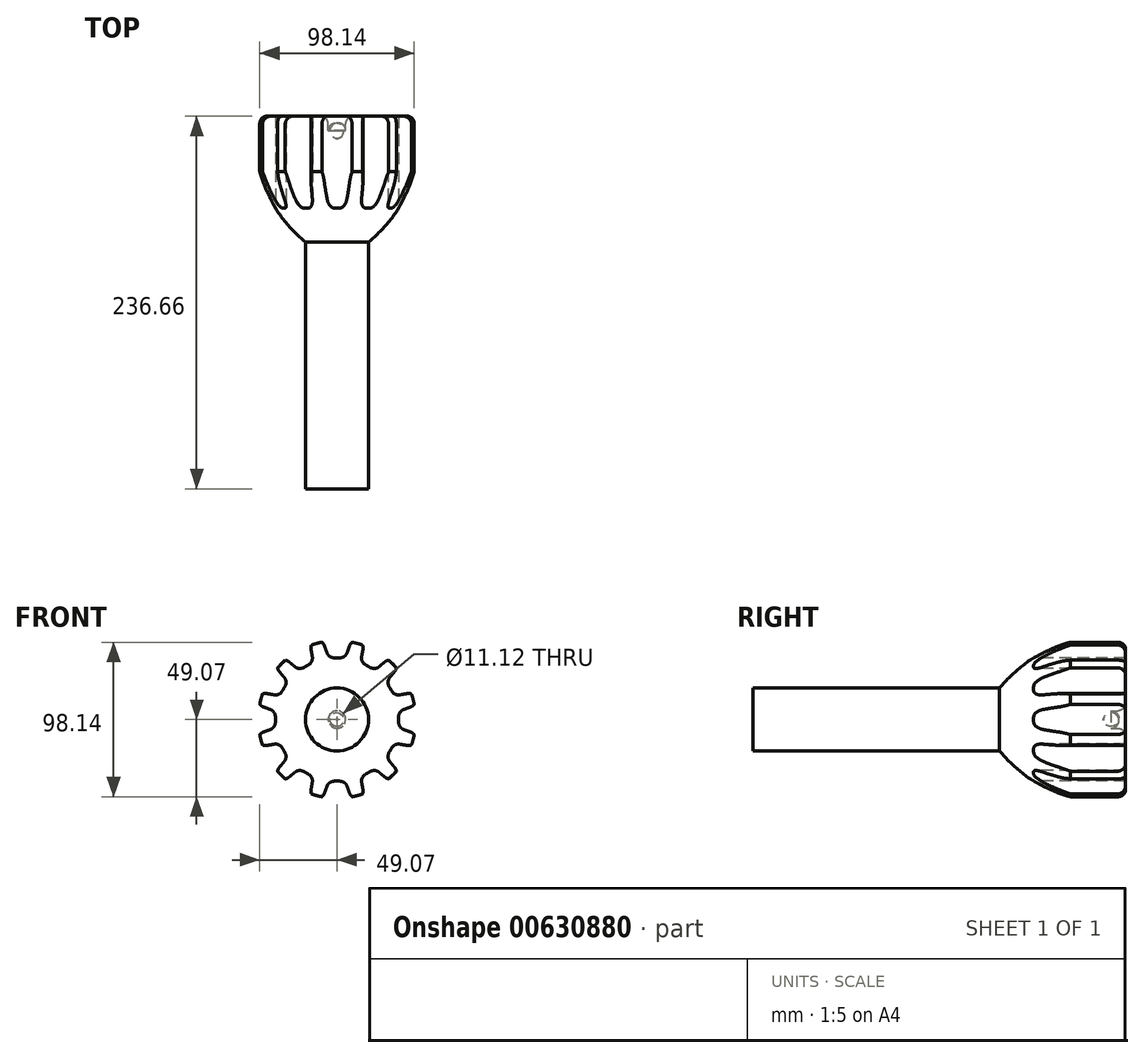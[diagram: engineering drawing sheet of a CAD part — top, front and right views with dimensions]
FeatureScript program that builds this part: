
annotation { "Feature Type Name" : "Feature", "Feature Type Description" : "" }
export const myFeature = defineFeature(function(context is Context, id is Id, definition is map)
    precondition{}
    {
        {
            var Q0;
            Q0=qCreatedBy(makeId("Right.planeOp"),FACE);
            var sketch = newSketch(context, id + "F0", { "sketchPlane" : qUnion([Q0])});
            skLineSegment(sketch, "E0.bottom", {"start": v(78.33, -10) * mm, "end": v(-78.33, -10) * mm});
            skLineSegment(sketch, "E0.top", {"start": v(78.33, 10) * mm, "end": v(-78.33, 10) * mm});
            skLineSegment(sketch, "E0.left", {"start": v(78.33, -10) * mm, "end": v(78.33, 10) * mm});
            skLineSegment(sketch, "E0.right", {"start": v(-78.33, -10) * mm, "end": v(-78.33, 10) * mm});
            skPoint(sketch, "E0.middle", {"position": v(0, 0) * mm});
            skArc(sketch, "E1", {"start": v(123.23, 40) * mm, "mid": v(98.58, 28.3) * mm, "end": v(78.33, 10) * mm});
            skLineSegment(sketch, "E2", {"start": v(123.23, 40) * mm, "end": v(153.33, 40) * mm});
            skLineSegment(sketch, "E3", {"start": v(158.33, 35) * mm, "end": v(158.33, 0.56) * mm});
            skLineSegment(sketch, "E4", {"start": v(153.33, -4.44) * mm, "end": v(149.1, -4.44) * mm});
            skLineSegment(sketch, "E5", {"start": v(144.1, -9.44) * mm, "end": v(144.1, -10) * mm});
            skLineSegment(sketch, "E6", {"start": v(144.1, -10) * mm, "end": v(78.33, -10) * mm});
            skPoint(sketch, "E7.visualSharp", {"position": v(158.33, 40) * mm});
            skArc(sketch, "E7.filletArc", {"start": v(158.33, 35) * mm, "mid": v(156.87, 38.54) * mm, "end": v(153.33, 40) * mm});
            skPoint(sketch, "E8.visualSharp", {"position": v(158.33, -4.44) * mm});
            skArc(sketch, "E8.filletArc", {"start": v(153.33, -4.44) * mm, "mid": v(156.87, -2.98) * mm, "end": v(158.33, 0.56) * mm});
            skPoint(sketch, "E9.visualSharp", {"position": v(144.1, -4.44) * mm});
            skArc(sketch, "E9.filletArc", {"start": v(149.1, -4.44) * mm, "mid": v(145.56, -5.9) * mm, "end": v(144.1, -9.44) * mm});
            skSolve(sketch);
        }
        {
            var Q0;
            Q0 = qSketchRegion(id + "F0", true);
            var Q1;
            Q1=sQuery(id+"F0.wireOp",EDGE,"E0.bottom");
            revolve(context, id + "F1", {"entities" : qUnion([Q0]), "axis" : qUnion([Q1]), "revolveType" : RevolveType.FULL});
        }
        {
            var Q0;
            Q0=qCreatedBy(makeId("Front.planeOp"),FACE);
            var sketch = newSketch(context, id + "F2", { "sketchPlane" : qUnion([Q0])});
            skLineSegment(sketch, "E10", {"start": v(0, 0) * mm, "end": v(0, 14.13) * mm});
            skLineSegment(sketch, "E11", {"start": v(0, 29.15) * mm, "end": v(0, 14.13) * mm});
            skLineSegment(sketch, "E12", {"start": v(0, 29.15) * mm, "end": v(-1.7, 29.15) * mm});
            skLineSegment(sketch, "E13", {"start": v(-6.4, 32.44) * mm, "end": v(-8, 36.84) * mm});
            skLineSegment(sketch, "E14", {"start": v(-17.5, 37.98) * mm, "end": v(0, 51.15) * mm});
            skPoint(sketch, "E15", {"position": v(-17.5, 37.98) * mm});
            skLineSegment(sketch, "E16", {"start": v(-17, 37.7) * mm, "end": v(-17.5, 37.98) * mm});
            skPoint(sketch, "E17.visualSharp", {"position": v(-5.2, 29.15) * mm});
            skArc(sketch, "E17.filletArc", {"start": v(-6.4, 32.44) * mm, "mid": v(-4.57, 30.05) * mm, "end": v(-1.7, 29.15) * mm});
            skPoint(sketch, "E18.visualSharp", {"position": v(-10.37, 43.35) * mm});
            skArc(sketch, "E18.filletArc", {"start": v(-8, 36.84) * mm, "mid": v(-12.23, 40.1) * mm, "end": v(-17, 37.7) * mm});
            skLineSegment(sketch, "E19.MirrorCS", {"start": v(0, 29.15) * mm, "end": v(1.7, 29.15) * mm});
            skArc(sketch, "E20.MirrorCS", {"start": v(6.4, 32.44) * mm, "mid": v(4.57, 30.05) * mm, "end": v(1.7, 29.15) * mm});
            skLineSegment(sketch, "E21.MirrorCS", {"start": v(6.4, 32.44) * mm, "end": v(8, 36.84) * mm});
            skPoint(sketch, "E22.MirrorP", {"position": v(10.37, 43.35) * mm});
            skArc(sketch, "E23.MirrorCS", {"start": v(8, 36.84) * mm, "mid": v(14.64, 39.74) * mm, "end": v(17.2, 32.96) * mm});
            skLineSegment(sketch, "E24.MirrorCS", {"start": v(15.31, 36.72) * mm, "end": v(17.5, 37.98) * mm});
            skLineSegment(sketch, "E25.MirrorCS", {"start": v(17.5, 37.98) * mm, "end": v(0, 51.15) * mm});
            skSolve(sketch);
        }
        {
            var Q0;
            Q0=makeQuery(id+"F2.imprint","IMPRINT",FACE,{"disambiguationData":[TD([[makeQuery(id+"F2.imprint","IMPRINT",EDGE,{"derivedFrom":sQuery(id+"F2.wireOp",EDGE,"E12")}),-1.0]])]});
            extrude(context, id + "F3", {"entities" : qUnion([Q0]), "operationType" : NewBodyOperationType.REMOVE, "oppositeDirection" : true, "depth" : 201.7 * mm, "offsetDistance" : 25 * mm});
        }
        {
            var Q0;
            Q0=makeQuery(id+"F3.boolean.opBoolean","COPY",FACE,{"derivedFrom":makeQuery(id+"F3.opExtrude","SWEPT_FACE",FACE,{"disambiguationData":[OSD([sQuery(id+"F2.wireOp",EDGE,"E18.filletArc")])]})});
            var Q1;
            Q1=makeQuery(id+"F3.boolean.opBoolean","COPY",FACE,{"derivedFrom":makeQuery(id+"F3.opExtrude","SWEPT_FACE",FACE,{"disambiguationData":[OSD([sQuery(id+"F2.wireOp",EDGE,"E13")])]})});
            var Q2;
            Q2=makeQuery(id+"F3.boolean.opBoolean","COPY",FACE,{"derivedFrom":makeQuery(id+"F3.opExtrude","SWEPT_FACE",FACE,{"disambiguationData":[OSD([sQuery(id+"F2.wireOp",EDGE,"E17.filletArc")])]})});
            var Q3;
            Q3=makeQuery(id+"F3.boolean.opBoolean","COPY",FACE,{"derivedFrom":makeQuery(id+"F3.opExtrude","SWEPT_FACE",FACE,{"disambiguationData":[OSD([sQuery(id+"F2.wireOp",EDGE,"E12"),sQuery(id+"F2.wireOp",EDGE,"E19.MirrorCS")])]})});
            var Q4;
            Q4=makeQuery(id+"F3.boolean.opBoolean","COPY",FACE,{"derivedFrom":makeQuery(id+"F3.opExtrude","SWEPT_FACE",FACE,{"disambiguationData":[OSD([sQuery(id+"F2.wireOp",EDGE,"E20.MirrorCS")])]})});
            var Q5;
            Q5=makeQuery(id+"F3.boolean.opBoolean","COPY",FACE,{"derivedFrom":makeQuery(id+"F3.opExtrude","SWEPT_FACE",FACE,{"disambiguationData":[OSD([sQuery(id+"F2.wireOp",EDGE,"E21.MirrorCS")])]})});
            var Q6;
            Q6=makeQuery(id+"F3.boolean.opBoolean","COPY",FACE,{"derivedFrom":makeQuery(id+"F3.opExtrude","SWEPT_FACE",FACE,{"disambiguationData":[OSD([sQuery(id+"F2.wireOp",EDGE,"E23.MirrorCS")])]})});
            var Q7;
            Q7=makeQuery(id+"F1.opRevolve","SWEPT_FACE",FACE,{"disambiguationData":[OSD([sQuery(id+"F0.wireOp",EDGE,"E2")])]});
            circularPattern(context, id + "F4", {"patternType" : PatternType.FACE, "faces" : qUnion([Q0, Q1, Q2, Q3, Q4, Q5, Q6]), "axis" : qUnion([Q7]), "angle" : 360 * degree, "instanceCount" : 24, "equalSpace" : true});
        }
    });
